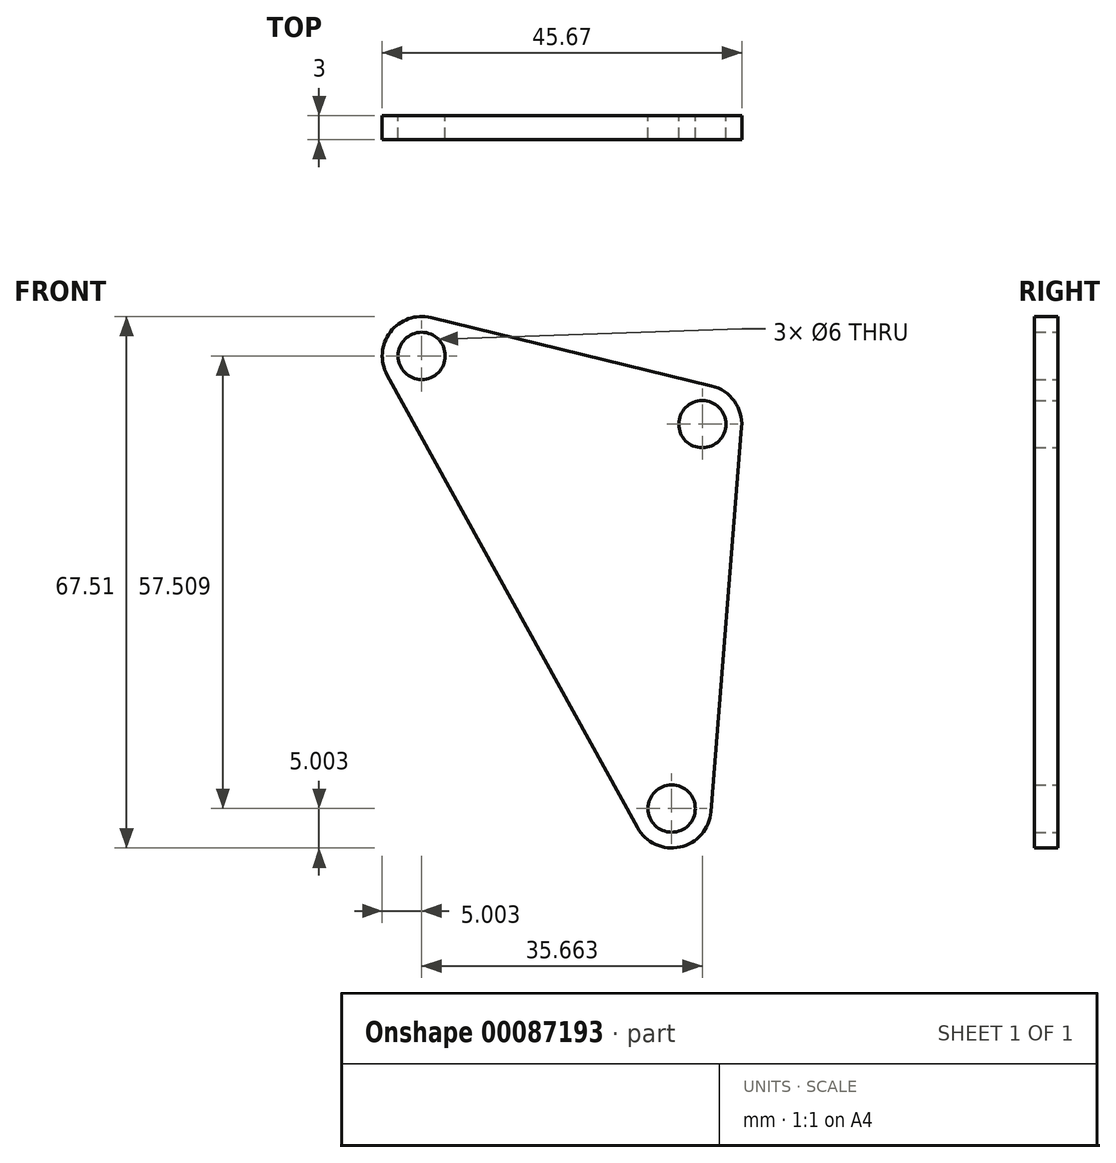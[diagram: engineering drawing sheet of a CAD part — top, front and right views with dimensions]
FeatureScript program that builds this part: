
annotation { "Feature Type Name" : "Feature", "Feature Type Description" : "" }
export const myFeature = defineFeature(function(context is Context, id is Id, definition is map)
    precondition{}
    {
        {
            var Q0;
            Q0=qCreatedBy(makeId("Front.planeOp"),FACE);
            var sketch = newSketch(context, id + "F0", { "sketchPlane" : qUnion([Q0])});
            skLineSegment(sketch, "E0", {"start": v(-33.79, 4.81) * mm, "end": v(-2.02, -52.7) * mm, "construction": true});
            skLineSegment(sketch, "E1", {"start": v(-2.02, -52.7) * mm, "end": v(1.88, -3.85) * mm, "construction": true});
            skLineSegment(sketch, "E2", {"start": v(1.88, -3.85) * mm, "end": v(-33.79, 4.81) * mm, "construction": true});
            skCircle(sketch, "E3", {"center": v(-33.79, 4.81) * mm, "radius": 3 * mm});
            skCircle(sketch, "E4", {"center": v(1.88, -3.85) * mm, "radius": 3 * mm});
            skCircle(sketch, "E5", {"center": v(-2.02, -52.7) * mm, "radius": 3 * mm});
            skLineSegment(sketch, "E6", {"start": v(-32.6, 9.67) * mm, "end": v(3.06, 1) * mm});
            skLineSegment(sketch, "E7", {"start": v(6.86, -4.25) * mm, "end": v(2.97, -53.1) * mm});
            skLineSegment(sketch, "E8", {"start": v(-6.4, -55.12) * mm, "end": v(-38.16, 2.4) * mm});
            skPoint(sketch, "E9.visualSharp", {"position": v(-43.67, 12.36) * mm});
            skArc(sketch, "E9.filletArc", {"start": v(-32.6, 9.67) * mm, "mid": v(-37.76, 7.85) * mm, "end": v(-38.16, 2.4) * mm});
            skPoint(sketch, "E10.visualSharp", {"position": v(1.64, -69.67) * mm});
            skArc(sketch, "E10.filletArc", {"start": v(-6.4, -55.12) * mm, "mid": v(-0.96, -57.58) * mm, "end": v(2.97, -53.1) * mm});
            skPoint(sketch, "E11.visualSharp", {"position": v(7.2, 0) * mm});
            skArc(sketch, "E11.filletArc", {"start": v(6.86, -4.25) * mm, "mid": v(5.93, -0.92) * mm, "end": v(3.06, 1) * mm});
            skSolve(sketch);
        }
        {
            var Q0;
            Q0 = qSketchRegion(id + "F0", true);
            extrude(context, id + "F1", {"entities" : qUnion([Q0]), "depth" : 3 * mm});
        }
    });
